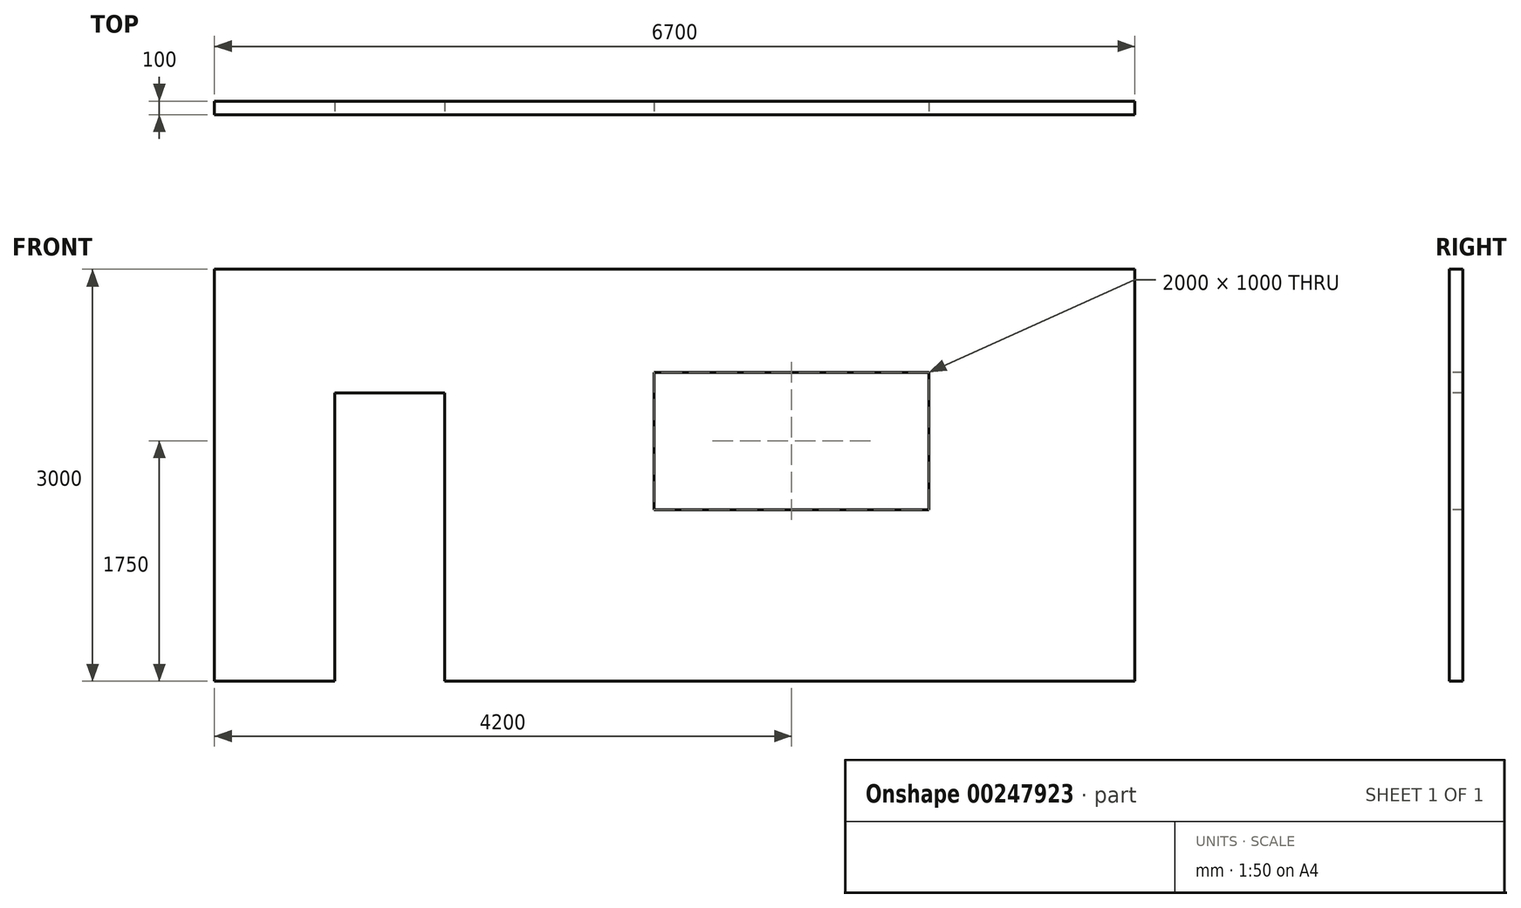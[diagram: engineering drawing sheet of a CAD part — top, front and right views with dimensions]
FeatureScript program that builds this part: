
annotation { "Feature Type Name" : "Feature", "Feature Type Description" : "" }
export const myFeature = defineFeature(function(context is Context, id is Id, definition is map)
    precondition{}
    {
        {
            var Q0;
            Q0=qCreatedBy(makeId("Front.planeOp"),FACE);
            var sketch = newSketch(context, id + "F0", { "sketchPlane" : qUnion([Q0])});
            skLineSegment(sketch, "E0.bottom", {"start": v(3350, 0) * mm, "end": v(-3350, 0) * mm});
            skLineSegment(sketch, "E0.top", {"start": v(3350, 3000) * mm, "end": v(-3350, 3000) * mm});
            skLineSegment(sketch, "E0.left", {"start": v(3350, 0) * mm, "end": v(3350, 3000) * mm});
            skLineSegment(sketch, "E0.right", {"start": v(-3350, 0) * mm, "end": v(-3350, 3000) * mm});
            skPoint(sketch, "E0.middle", {"position": v(0, 1500) * mm});
            skSolve(sketch);
        }
        {
            var Q0;
            Q0=makeQuery(id+"F0.imprint","IMPRINT",FACE,{"disambiguationData":[TD([[makeQuery(id+"F0.imprint","IMPRINT",EDGE,{"derivedFrom":sQuery(id+"F0.wireOp",EDGE,"E0.bottom")}),-1.0]])]});
            extrude(context, id + "F1", {"entities" : qUnion([Q0]), "endBound" : BoundingType.SYMMETRIC, "depth" : 100 * mm});
        }
        {
            var Q0;
            Q0=makeQuery(id+"F1.opExtrude","CAP_FACE",FACE,{"disambiguationData":[OSD([sQuery(id+"F0.wireOp",EDGE,"E0.bottom"),sQuery(id+"F0.wireOp",EDGE,"E0.top"),sQuery(id+"F0.wireOp",EDGE,"E0.left"),sQuery(id+"F0.wireOp",EDGE,"E0.right")])],"isStart":false});
            var sketch = newSketch(context, id + "F2", { "sketchPlane" : qUnion([Q0])});
            skLineSegment(sketch, "E1.bottom", {"start": v(1850, 1250) * mm, "end": v(-150, 1250) * mm});
            skLineSegment(sketch, "E1.top", {"start": v(1850, 2250) * mm, "end": v(-150, 2250) * mm});
            skLineSegment(sketch, "E1.left", {"start": v(1850, 1250) * mm, "end": v(1850, 2250) * mm});
            skLineSegment(sketch, "E1.right", {"start": v(-150, 1250) * mm, "end": v(-150, 2250) * mm});
            skPoint(sketch, "E1.middle", {"position": v(850, 1750) * mm});
            skLineSegment(sketch, "E2", {"start": v(-1650, 3000) * mm, "end": v(-1650, 0) * mm, "construction": true});
            skLineSegment(sketch, "E3", {"start": v(-1650, 0) * mm, "end": v(3350, 0) * mm, "construction": true});
            skPoint(sketch, "E4", {"position": v(850, 0) * mm});
            skLineSegment(sketch, "E5.bottom", {"start": v(-1675, 0) * mm, "end": v(-2475, 0) * mm});
            skLineSegment(sketch, "E5.top", {"start": v(-1675, 2100) * mm, "end": v(-2475, 2100) * mm});
            skLineSegment(sketch, "E5.left", {"start": v(-1675, 0) * mm, "end": v(-1675, 2100) * mm});
            skLineSegment(sketch, "E5.right", {"start": v(-2475, 0) * mm, "end": v(-2475, 2100) * mm});
            skPoint(sketch, "E5.middle", {"position": v(-2075, 1050) * mm});
            skLineSegment(sketch, "E6", {"start": v(-2500, 3000) * mm, "end": v(-2500, 0) * mm, "construction": true});
            skLineSegment(sketch, "E7", {"start": v(-3350, 0) * mm, "end": v(-1650, 0) * mm, "construction": true});
            skLineSegment(sketch, "E8", {"start": v(-2500, 3000) * mm, "end": v(-1650, 3000) * mm, "construction": true});
            skPoint(sketch, "E9", {"position": v(-2075, 3000) * mm});
            skSolve(sketch);
        }
        {
            var Q0;
            Q0=makeQuery(id+"F2.imprint","IMPRINT",FACE,{"disambiguationData":[TD([[makeQuery(id+"F2.imprint","IMPRINT",EDGE,{"derivedFrom":sQuery(id+"F2.wireOp",EDGE,"E1.bottom")}),-1.0]])]});
            var Q1;
            Q1=makeQuery(id+"F2.imprint","IMPRINT",FACE,{"disambiguationData":[TD([[makeQuery(id+"F2.imprint","IMPRINT",EDGE,{"derivedFrom":sQuery(id+"F2.wireOp",EDGE,"E5.bottom")}),-1.0]])]});
            extrude(context, id + "F3", {"entities" : qUnion([Q0, Q1]), "operationType" : NewBodyOperationType.REMOVE, "endBound" : BoundingType.THROUGH_ALL, "oppositeDirection" : true, "depth" : 25 * mm});
        }
    });
